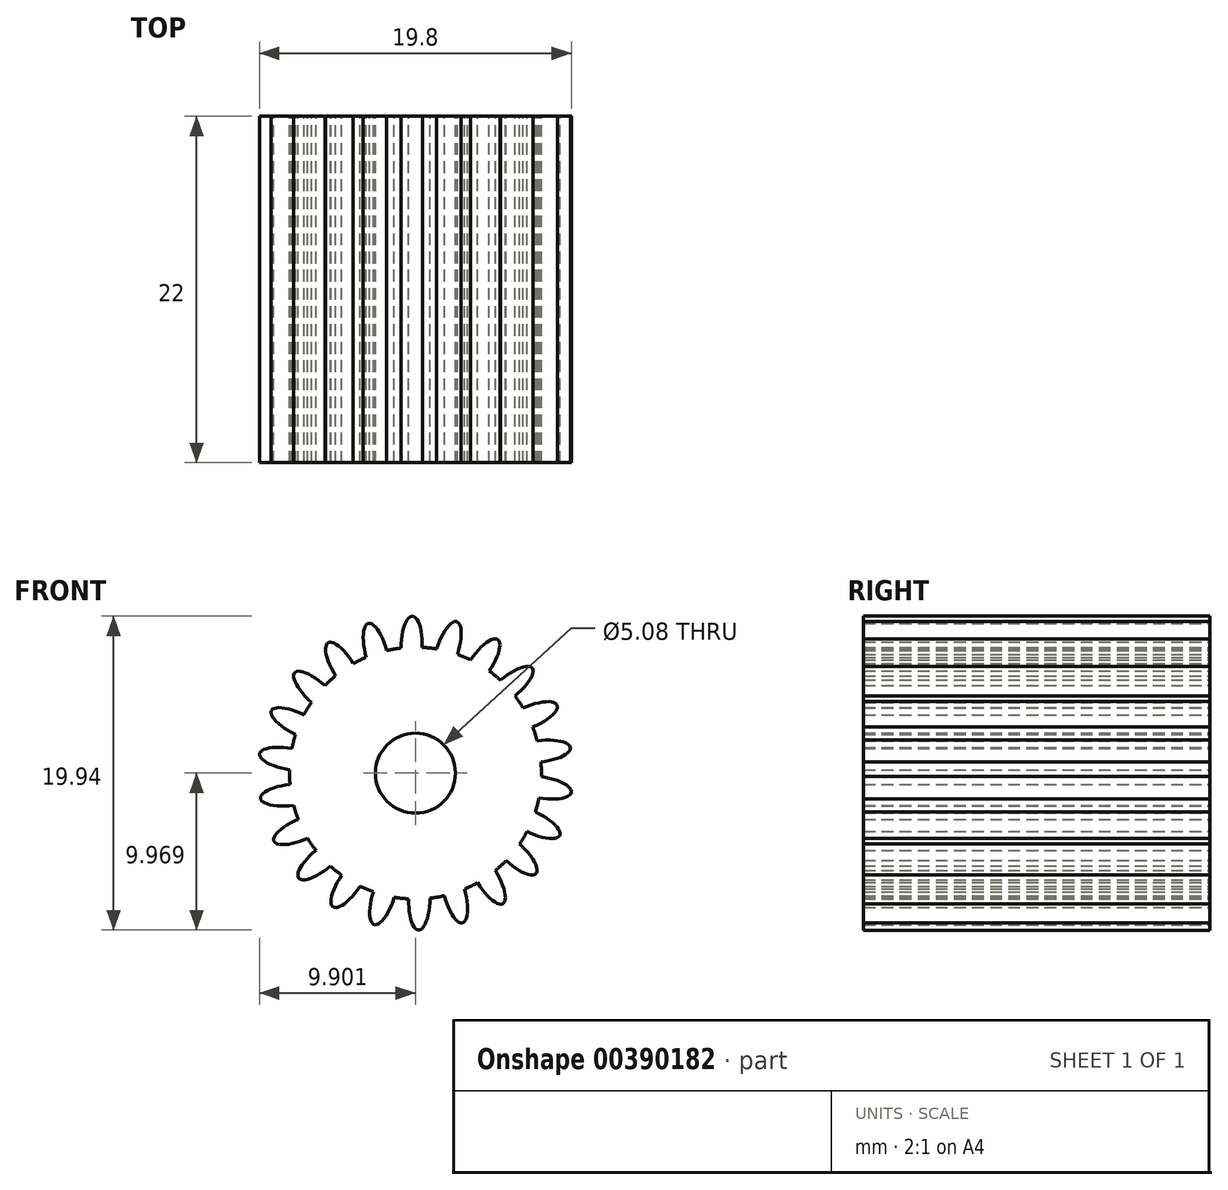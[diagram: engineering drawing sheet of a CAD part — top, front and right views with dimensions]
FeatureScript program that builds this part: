
annotation { "Feature Type Name" : "Feature", "Feature Type Description" : "" }
export const myFeature = defineFeature(function(context is Context, id is Id, definition is map)
    precondition{}
    {
        {
            var Q0;
            Q0=qCreatedBy(makeId("Front.planeOp"),FACE);
            var sketch = newSketch(context, id + "F0", { "sketchPlane" : qUnion([Q0])});
            skCircle(sketch, "E0", {"center": v(0.02, -0.42) * mm, "radius": 8 * mm});
            skLineSegment(sketch, "E1", {"start": v(0.02, -0.42) * mm, "end": v(-1.13, 7.5) * mm});
            skLineSegment(sketch, "E2", {"start": v(0.02, -0.42) * mm, "end": v(0.12, 7.58) * mm});
            skEllipticalArc(sketch, "E3.38.0", {});
            skCircle(sketch, "E4", {"center": v(0.02, -0.42) * mm, "radius": 2.54 * mm});
            skEllipticalArc(sketch, "E5.1.0", {});
            skEllipticalArc(sketch, "E5.2.0", {});
            skEllipticalArc(sketch, "E5.3.0", {});
            skEllipticalArc(sketch, "E5.4.0", {});
            skEllipticalArc(sketch, "E5.5.0", {});
            skEllipticalArc(sketch, "E5.6.0", {});
            skEllipticalArc(sketch, "E5.7.0", {});
            skEllipticalArc(sketch, "E5.8.0", {});
            skEllipticalArc(sketch, "E5.9.0", {});
            skEllipticalArc(sketch, "E5.10.0", {});
            skEllipticalArc(sketch, "E5.11.0", {});
            skEllipticalArc(sketch, "E5.12.0", {});
            skEllipticalArc(sketch, "E5.13.0", {});
            skEllipticalArc(sketch, "E5.14.0", {});
            skEllipticalArc(sketch, "E5.15.0", {});
            skEllipticalArc(sketch, "E5.16.0", {});
            skEllipticalArc(sketch, "E5.17.0", {});
            skEllipticalArc(sketch, "E5.18.0", {});
            skEllipticalArc(sketch, "E5.19.0", {});
            skEllipticalArc(sketch, "E5.20.0", {});
            skEllipticalArc(sketch, "E5.21.0", {});
            const initialGuessF0  = {"E3.38.0": [0.002036120399755269, 0.0073205969644864755, -0.3090169943749474, -0.9510565162951536, 0.0019768298493211675, 0.0006797314705727096, 1.5766588321977384, 4.747653305813112], "E5.1.0": [-0.00022669867967855563, 0.007574662292885675, -0.02855605079369622, -0.9995921928281893, 0.0019768298493211675, 0.0006797314705727096, 1.5766588321977386, 4.747653305813111], "E5.2.0": [-0.0024694361615308, 0.0071809263854053056, 0.25421833419348694, -0.9671468547019572, 0.0019768298493211675, 0.0006797314705727096, 1.5766588321977386, 4.747653305813111], "E5.3.0": [-0.004510398793095173, 0.006171287383631821, 0.5163974616389619, -0.856349030251589, 0.0019768298493211675, 0.0006797314705727096, 1.5766588321977386, 4.747653305813111], "E5.4.0": [-0.006184239920034473, 0.004627540234934563, 0.7367411378764049, -0.6761749002740194, 0.0019768298493211675, 0.0006797314705727096, 1.5766588321977386, 4.747653305813111], "E5.5.0": [-0.007355354888960557, 0.002674750152283181, 0.8973984286913584, -0.4412211012432212, 0.0019768298493211675, 0.0006797314705727096, 1.5766588321977386, 4.747653305813111], "E5.6.0": [-0.007928866929979935, 0.00047112057448429, 0.9853538358476931, -0.1705221926326239, 0.0019768298493211675, 0.0006797314705727096, 1.5766588321977386, 4.747653305813111], "E5.7.0": [-0.007858313508336654, -0.0018048235355585646, 0.9934817353485503, 0.11399140989054057, 0.0019768298493211675, 0.0006797314705727096, 1.5766588321977386, 4.747653305813111], "E5.8.0": [-0.0071494104426549, -0.003968698721610511, 0.9211236531148501, 0.38927010631739145, 0.0019768298493211675, 0.0006797314705727096, 1.5766588321977386, 4.747653305813111], "E5.9.0": [-0.005859588843307343, -0.005845200685158868, 0.7741416106390826, 0.6330124538088703, 0.0019768298493211675, 0.0006797314705727096, 1.5766588321977386, 4.747653305813111], "E5.10.0": [-0.004093342385408703, -0.007282306397103836, 0.5644432188667692, 0.825471896962774, 0.0019768298493211675, 0.0006797314705727096, 1.5766588321977386, 4.747653305813111], "E5.11.0": [-0.0019937618527057924, -0.00816359009946039, 0.30901699437494795, 0.9510565162951534, 0.0019768298493211675, 0.0006797314705727096, 1.5766588321977386, 4.747653305813111], "E5.12.0": [0.00026905722672803474, -0.00841765542785959, 0.028556050793696552, 0.9995921928281893, 0.0019768298493211675, 0.0006797314705727096, 1.5766588321977386, 4.747653305813111], "E5.13.0": [0.002511794708580281, -0.00802391952037922, -0.25421833419348694, 0.9671468547019572, 0.0019768298493211675, 0.0006797314705727096, 1.5766588321977386, 4.747653305813111], "E5.14.0": [0.004552757340144654, -0.007014280518605736, -0.5163974616389618, 0.856349030251589, 0.0019768298493211675, 0.0006797314705727096, 1.5766588321977386, 4.747653305813111], "E5.15.0": [0.00622659846708395, -0.005470533369908482, -0.7367411378764044, 0.67617490027402, 0.0019768298493211675, 0.0006797314705727096, 1.5766588321977386, 4.747653305813111], "E5.16.0": [0.007397713436010037, -0.003517743287257096, -0.8973984286913584, 0.44122110124322134, 0.0019768298493211675, 0.0006797314705727096, 1.5766588321977386, 4.747653305813111], "E5.17.0": [0.007971225477029416, -0.0013141137094582053, -0.9853538358476931, 0.170522192632624, 0.0019768298493211675, 0.0006797314705727096, 1.5766588321977386, 4.747653305813111], "E5.18.0": [0.007900672055386136, 0.000961830400584648, -0.9934817353485503, -0.11399140989054024, 0.0019768298493211675, 0.0006797314705727096, 1.5766588321977386, 4.747653305813111], "E5.19.0": [0.007191768989704384, 0.003125705586636593, -0.9211236531148503, -0.3892701063173909, 0.0019768298493211675, 0.0006797314705727096, 1.5766588321977386, 4.747653305813111], "E5.20.0": [0.005901947390356822, 0.005002207550184956, -0.7741416106390825, -0.6330124538088706, 0.0019768298493211675, 0.0006797314705727096, 1.5766588321977386, 4.747653305813111], "E5.21.0": [0.004135700932458185, 0.006439313262129921, -0.5644432188667692, -0.825471896962774, 0.0019768298493211675, 0.0006797314705727096, 1.5766588321977386, 4.747653305813111]};
            skSetInitialGuess(sketch, initialGuessF0);
            skSolve(sketch);
        }
        {
            var Q0;
            Q0=qSketchRegion(id+"F0",true);
            extrude(context, id + "F1", {"entities" : qUnion([Q0]), "depth" : 22 * mm});
        }
    });
